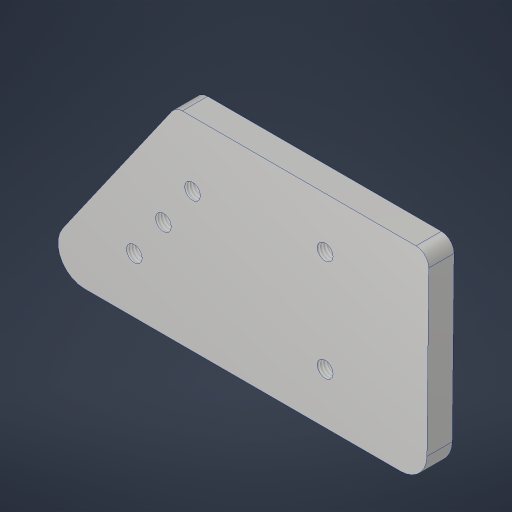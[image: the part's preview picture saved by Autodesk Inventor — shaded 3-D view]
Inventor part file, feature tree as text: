
AUTODESK INVENTOR PART (.ipt)
format: ipt  version: 2023.4 (Build 274418000, 418)  size: 254,464 bytes
history: native  units: in
note: dims shown in document units (in); Inventor stores cm internally (conversion verified against a paired STEP export)
features: sketch x5, extrude x3, hole x3, fillet x2, projected_geometry x1
ambient origin geometry x8: Origin, YZ Plane, XZ Plane, XY Plane, X Axis, Y Axis, Z Axis, Center Point
bodies: Solid1 (feature_tree)
feature tree (14):
  sketch  "Sketch1"  dims[d0=2.0in d1=15.25in]
  sketch  "Sketch2"  dims[d2=1.0in d3=17.0in d5=0.3779in]
  extrude  "Extrusion1"  Depth=2.0in
  hole  "Hole1"  [1 undecoded]
  fillet  "Fillet1"  Radius=0.3779in
  sketch  "Sketch3"  dims[d6=0.88in d7=1.875in]
  extrude  "Extrusion2"  Depth=1.875in
  hole  "Hole2"  [1 undecoded]
  extrude  "Extrusion3"  Depth=0.25in
  fillet  "Fillet2"  Radius=1.0in
  hole  "Hole3"  [1 undecoded]
  projected_geometry  "Projected Loop1"
  sketch  "Sketch4"  dims[d8=0.625in d10=0.5in]
  sketch  "Sketch5"  dims[d11=17.0in d12=4.0in d13=1.0in d14=0.5in d15=0.5in d16=0.5in d18=0.25in d19=0.0in d20=0.156in d21=0.38in d22=0.385in d23=0.25in d24=0.5635in d25=1.0in d26=0.8108in d27=0.26in d28=1.875in d29=2.5in d30=1.5748in d32=360.0deg d34=0.125in d35=0.0in d36=0.156in d37=0.38in d38=0.385in d39=0.25in d40=0.5635in d41=1.0in d42=0.8108in d43=2.0in d44=0.0in d45=0.0in d46=0.125in d47=1.0in d48=0.5in d49=0.156in d50=0.38in d51=0.385in d52=0.25in d53=0.5635in d54=1.0in d55=0.8108in d56=1.25in]
note: 3 required parameter values undecoded (feature->parameter linkage not recoverable at this tier; creation-order binding heuristic only, values carry confidence <= 0.55)
